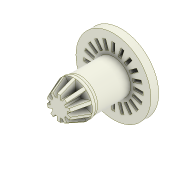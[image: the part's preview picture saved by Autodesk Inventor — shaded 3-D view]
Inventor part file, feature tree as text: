
AUTODESK INVENTOR PART (.ipt)
format: ipt  version: 2022 (Build 260153000, 153)  size: 380,416 bytes
history: native  units: mm
features: extrude x8, sketch x8, thicken_offset x2, chamfer x1, hole x1, pattern_circular x1, fillet x1, other x1
ambient origin geometry x8: Origin, YZ Plane, XZ Plane, XY Plane, X Axis, Y Axis, Z Axis, Center Point
bodies: Solid1 (feature_tree)
feature tree (23):
  extrude  "Adapter"  Depth=1.0mm TaperAngle=0.0deg
  extrude  "Motor Shaft Profile"  Depth=13.0mm
  chamfer  "Chamfer1"  Distance=12.0mm
  thicken_offset  "Thicken5"
  thicken_offset  "Thicken6"
  hole  "Hole6"  [1 undecoded]
  extrude  "Extrusion5"  Depth=0.2mm
  extrude  "Extrusion6"  Depth=2.0mm
  extrude  "Extrusion7"  Depth=7.5mm
  pattern_circular  "Circular Pattern1"  [2 undecoded]
  extrude  "Extrusion8"  TaperAngle=0.0deg  [1 undecoded]
  fillet  "Fillet1"  Radius=100.0mm
  extrude  "Extrusion9"  Depth=1.0mm
  extrude  "Extrusion10"  Depth=10.0mm TaperAngle=0.0deg
  sketch  "Sketch1"  dims[d1=11.0mm d2=1.0mm d3=0.0mm]
  sketch  "Sketch6"  dims[d4=13.0mm d5=0.0mm d35=6.0mm]
  sketch  "Sketch9"  dims[d36=5.5mm d37=12.0mm d38=0.0mm]
  sketch  "Sketch10"  dims[d39=0.2mm d40=0.1mm d48=0.5mm d49=2.0mm d50=45.0deg]
  sketch  "Sketch11"  dims[d58=0.2mm d59=0.2mm]
  sketch  "Sketch12"  dims[d67=2.85mm d68=7.0mm d69=4.0mm d70=2.0mm d71=90.0deg d72=10.4mm d73=20.594885mm d74=11.5mm]
  sketch  "Sketch13"  dims[d75=1.0mm d76=0.0mm d77=7.5mm]
  other  "Encoder Wheel"
  sketch  "Sketch15"  dims[d78=6.0mm d79=1.0mm d80=0.0mm d81=0.0mm d82=0.0mm d83=100.0mm d84=360.0deg d86=5.0mm d87=10.0mm d88=0.0mm d89=2.0mm d90=24.0mm d91=2.5mm d92=0.0mm d93=1.0mm d94=9.5mm d95=6.5mm d96=200.0mm d98=360.0deg d100=0.0mm d101=0.0mm d41=1.0mm d42=1.0mm d43=1.0mm d44=0.15mm d45=0.25mm d46=0.375mm d47=14.3117mm d51=0.75mm d52=0.375mm d60=0.5mm d61=0.872665mm]
note: 4 required parameter values undecoded (feature->parameter linkage not recoverable at this tier; creation-order binding heuristic only, values carry confidence <= 0.55)
